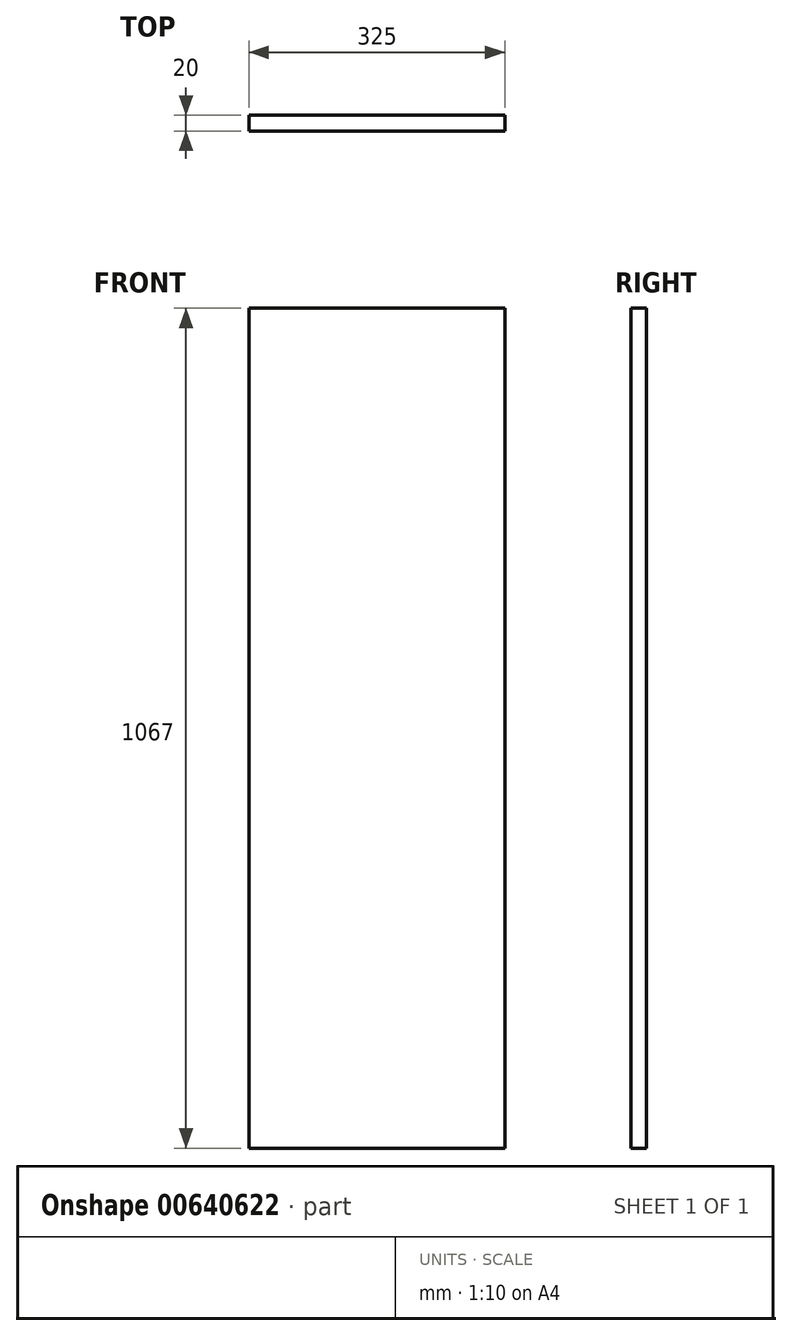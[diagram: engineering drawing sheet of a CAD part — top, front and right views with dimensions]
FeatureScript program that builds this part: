
annotation { "Feature Type Name" : "Feature", "Feature Type Description" : "" }
export const myFeature = defineFeature(function(context is Context, id is Id, definition is map)
    precondition{}
    {
        {
            var Q0;
            Q0=qCreatedBy(makeId("Front.planeOp"),FACE);
            var sketch = newSketch(context, id + "F0", { "sketchPlane" : qUnion([Q0])});
            skLineSegment(sketch, "E0.bottom", {"start": v(0, 0) * mm, "end": v(-325, 0) * mm});
            skLineSegment(sketch, "E0.top", {"start": v(0, 1067) * mm, "end": v(-325, 1067) * mm});
            skLineSegment(sketch, "E0.left", {"start": v(0, 0) * mm, "end": v(0, 1067) * mm});
            skLineSegment(sketch, "E0.right", {"start": v(-325, 0) * mm, "end": v(-325, 1067) * mm});
            skSolve(sketch);
        }
        {
            var Q0;
            Q0 = qSketchRegion(id + "F0", true);
            extrude(context, id + "F1", {"entities" : qUnion([Q0]), "depth" : 20 * mm, "offsetDistance" : 25 * mm});
        }
    });
